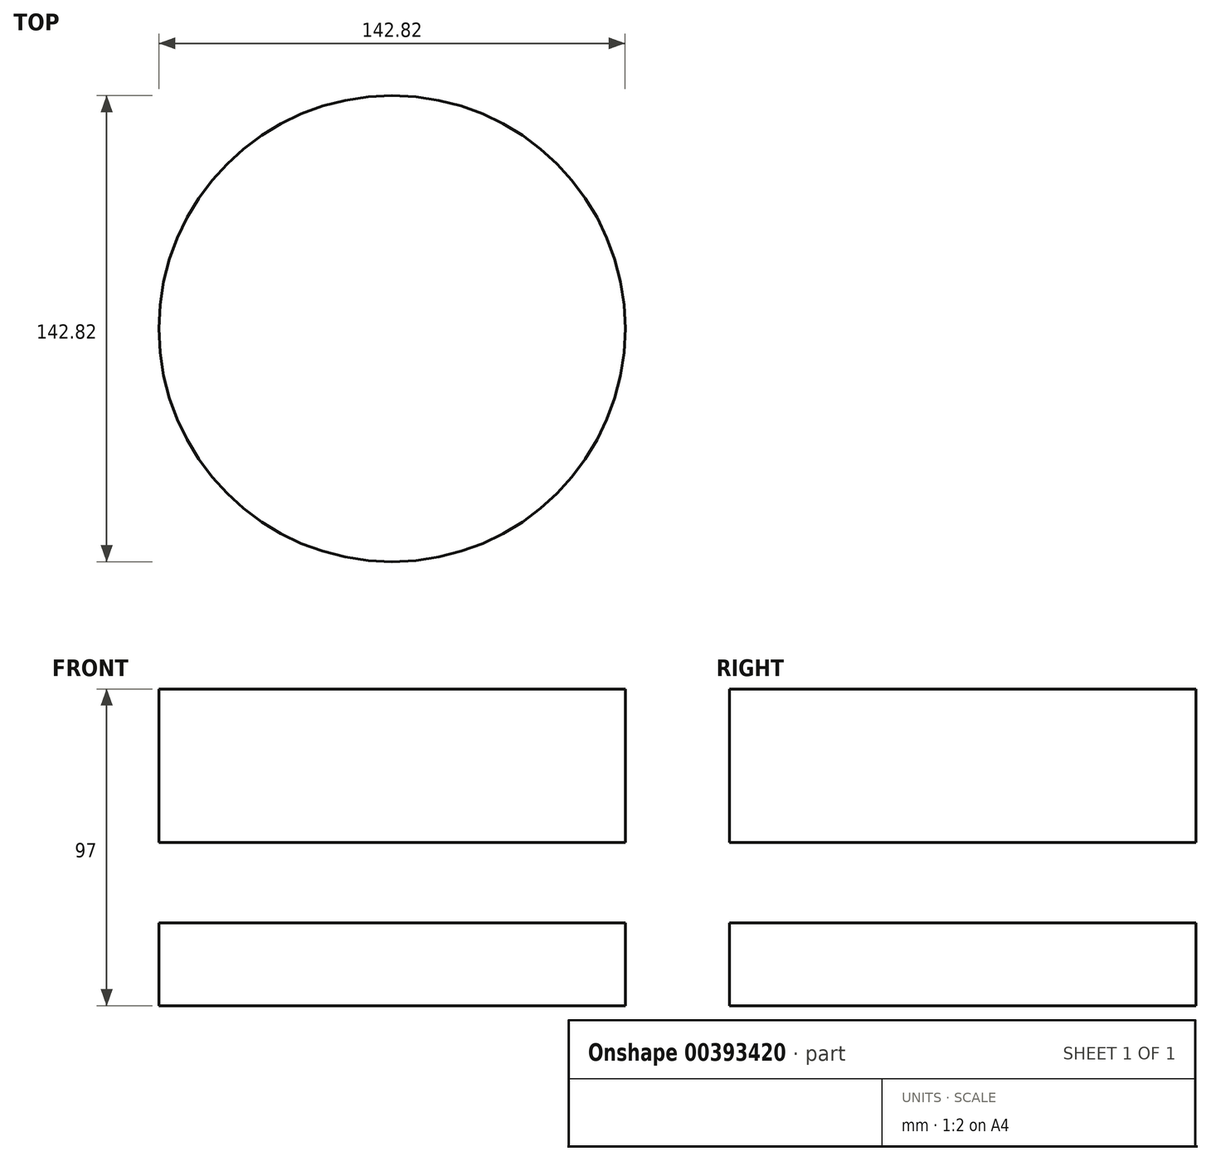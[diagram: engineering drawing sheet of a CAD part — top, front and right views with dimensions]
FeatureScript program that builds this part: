
annotation { "Feature Type Name" : "Feature", "Feature Type Description" : "" }
export const myFeature = defineFeature(function(context is Context, id is Id, definition is map)
    precondition{}
    {
        {
            var Q0;
            Q0=qCreatedBy(makeId("Top.planeOp"),FACE);
            var sketch = newSketch(context, id + "F0", { "sketchPlane" : qUnion([Q0])});
            skCircle(sketch, "E0", {"center": v(0, 0) * mm, "radius": 71.41 * mm});
            skSolve(sketch);
        }
        {
            var Q0;
            Q0=makeQuery(id+"F0.imprint","IMPRINT",FACE,{"disambiguationData":[TD([[makeQuery(id+"F0.imprint","IMPRINT",EDGE,{"derivedFrom":sQuery(id+"F0.wireOp",EDGE,"E0")}),1.0]])]});
            extrude(context, id + "F1", {"entities" : qUnion([Q0]), "depth" : 25.4 * mm});
        }
        {
            var Q0;
            Q0=qCreatedBy(makeId("Top.planeOp"),FACE);
            cPlane(context, id + "F2", {"entities" : qUnion([Q0]), "cplaneType" : CPlaneType.OFFSET, "offset" : 50 * mm, "width" : 152.4 * mm, "height" : 152.4 * mm});
        }
        {
            var Q0;
            Q0=qCreatedBy(id+"F2.planeOp",FACE);
            var sketch = newSketch(context, id + "F3", { "sketchPlane" : qUnion([Q0])});
            skCircle(sketch, "E1.0", {"center": v(0, 0) * mm, "radius": 71.41 * mm});
            skSolve(sketch);
        }
        {
            var Q0;
            Q0=makeQuery(id+"F3.imprint","IMPRINT",FACE,{"disambiguationData":[TD([[makeQuery(id+"F3.imprint","IMPRINT",EDGE,{"derivedFrom":sQuery(id+"F3.wireOp",EDGE,"E1.0")}),1.0]])]});
            extrude(context, id + "F4", {"entities" : qUnion([Q0]), "depth" : 47 * mm});
        }
    });
